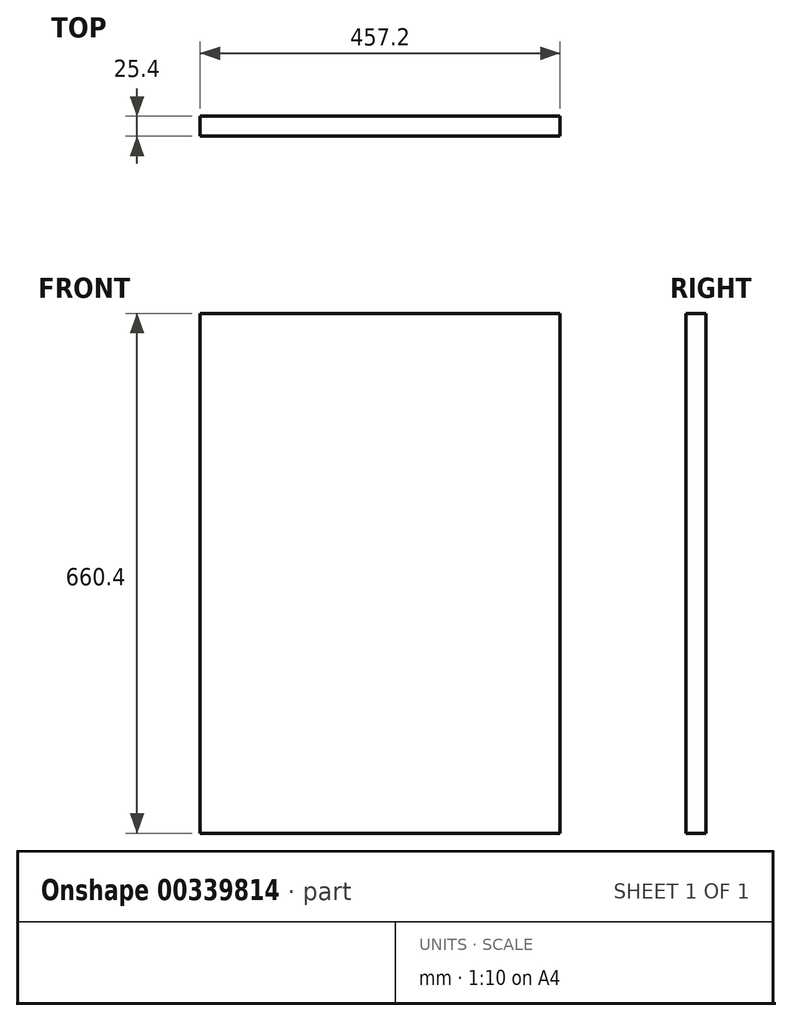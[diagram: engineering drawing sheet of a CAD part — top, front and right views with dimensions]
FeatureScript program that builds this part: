
annotation { "Feature Type Name" : "Feature", "Feature Type Description" : "" }
export const myFeature = defineFeature(function(context is Context, id is Id, definition is map)
    precondition{}
    {
        {
            var Q0;
            Q0=qCreatedBy(makeId("Front.planeOp"),FACE);
            var sketch = newSketch(context, id + "F0", { "sketchPlane" : qUnion([Q0])});
            skLineSegment(sketch, "E0.bottom", {"start": v(-37.45, 604.82) * mm, "end": v(419.75, 604.82) * mm});
            skLineSegment(sketch, "E0.top", {"start": v(-37.45, -55.58) * mm, "end": v(419.75, -55.58) * mm});
            skLineSegment(sketch, "E0.left", {"start": v(-37.45, 604.82) * mm, "end": v(-37.45, -55.58) * mm});
            skLineSegment(sketch, "E0.right", {"start": v(419.75, 604.82) * mm, "end": v(419.75, -55.58) * mm});
            skSolve(sketch);
        }
        {
            var Q0;
            Q0 = qSketchRegion(id + "F0", true);
            extrude(context, id + "F1", {"entities" : qUnion([Q0]), "depth" : 25.4 * mm});
        }
    });
